# Revit family: NBS_Allermuir_OffcChrs_Folk_SideChair
name_source: partatom
category: Furniture
revit_build: Autodesk Revit 2018 (Build: 20190510_1515(x64)
units: mm (PartAtom-declared; Revit-internal decimal feet)

## family parameters
Always vertical = Yes
Cut with Voids When Loaded = No
Room Calculation Point = No
Shared = No
Work Plane-Based = No

## types (2) — shared parameters
AssetType = Movable
Category = Pr_40_50_12_57:Office chairs
CodePerformance = BS EN 16139 Level 1
DurationUnit = year
ExpectedLife = 10
Finish = Off-Black powder coat, White powder coat, Crayon Grey powder coat, Pistachio powder coat, Seattle Green powder coat, Aubergine powder coat, Off-Black plastic, White plastic, Crayon Grey plastic, Pistachio plastic, Seattle Green plastic, Aubergine plastic, Clear Beech, Clear Oak, American Cherry, American Walnut, Dark Walnut, Wenge, Off-Black colour wash, White colour wash, Crayon Grey colour wash, Pistachio colour wash, Seattle Green colour wash, Aubergine colour wash
FrameFinish = Off black, White, Crayon grey, Pistachio, Seattle green, Aubergine
FrameMaterial = NBS_Allermuir_Aluminium_BlackPowderCoat
IfcExportAs = IfcFurnitureType
IfcExportType = CHAIR
IsBuiltIn = No
LegMaterial = NBS_Allermuir_Beech_ClearFinish
ManufacturerName = Allermuir
ManufacturerURL = www.allermuir.co.uk
Material = Solid Wood, Polypropylene, Aluminium Casting
ModelReference = Folk_SideChair
NBSCertification = www.nationalbimlibrary.com/cert/3pjwsa5j
NBSDescription = Office chairs
NBSReference = 45-35-20/330
NominalDepth = 505 mm
NominalHeight = 790 mm
NominalLength = 475 mm
NominalWidth = 475 mm
ProductInformation = https://www.allermuir.com
SeatDepth = 435 mm
SeatWidth = 455 mm
SeatingHeight = 450 mm  [stored 1.47638 ft]
Size = 505 x 790 x 475 mm
Status = UNSET
Style = Chair
SustainabilityPerformance = 99% recyclable
Uniclass2015Code = Pr_40_50_12_57
Uniclass2015Title = Office chairs
Uniclass2015Version = Products v1.15
Version = 1
WarrantyDescription = Allermuir warrant that its manufactured products are free from manufacturing defects - in materials or workmanship - for a period of five (5) years. , Allermuir will repair, or replace (at Allermuir's sole discretion) with comparable free of charge materials / components, any product / component which fails under normal use in a single shift environment, as a result of a defect in the materials and/ or workmanship
WarrantyDurationParts = 5
WarrantyDurationUnit = year
WoodStains = Clear Oak, American Cherry, American Walnut, Dark Walnut, Wenge
zero-valued in all types: HighestSeatingHeight, LowestSeatingHeight

## per-type parameters (varying)
| type | BIMObjectName | Color | Description | Features | ModelNumber | Name | SeatMaterial |
| Folk_SideChair_FLK101 | NBS_Allermuir_OfficeChairs_Folk_SideChair_FLK101 | Off black, White, Crayon grey, Pistachio, Seattle green, Aubergine | Chair - Wood seat and back | Beech ply seat with a clear finish, Beech ply back with a clear finish, Cast Aluminum frame finished in Off-Black powder coat, Solid Beech legs with a clear finish, Plastic glides, Stacks up to 4 high, Cast Aluminum frame available in a selection of powder coat finishes, Beech ply seat, back and solid Beech legs available in a selection of color washes or stains, Solid Beech legs available in a selection of color washes or stains, Oak ply seat, back and solid Oak legs with a clear finish, Solid Oak legs available in a selection of color washes, Plastic glides with felt | FLK101 | OfficeChairs_FLK101_Folk_Allermuir | NBS_Allermuir_Beech_ClearFinish |
| Folk_SideChair_FLK103 | NBS_Allermuir_OfficeChairs_Folk_SideChair_FLK103 | Off-Black, White, Crayon Grey, Pistachio, Haze Blue, Aubergine, Seattle Green, Red | Chair - Plastic seat and back | Plastic seat — Color: Off-Black, Plastic back — Color: Off-Black, Cast Aluminum frame finished in Off-Black powder coat, Solid Beech legs with a clear finish, Plastic glides, Stacks up to 4 high, Cast Aluminum frame available in a selection of powder coat finishes, Plastic seat and back available in a selection of colors, Solid Beech legs available in a selection of color washes or stains, Solid Oak legs with a clear finish, Solid Oak legs available in a selection of color washes, Plastic glides with felt | FLK103 | OfficeChairs_FLK103_Folk_Allermuir | NBS_Allermuir_Plastic_Black |

note: [stored X ft] marks values corroborated as IEEE doubles in the binary element streams (Revit-internal decimal feet)

## geometry (parser evidence)
native form markers: Sweep x6
no freeform markers — native parametric forms only
